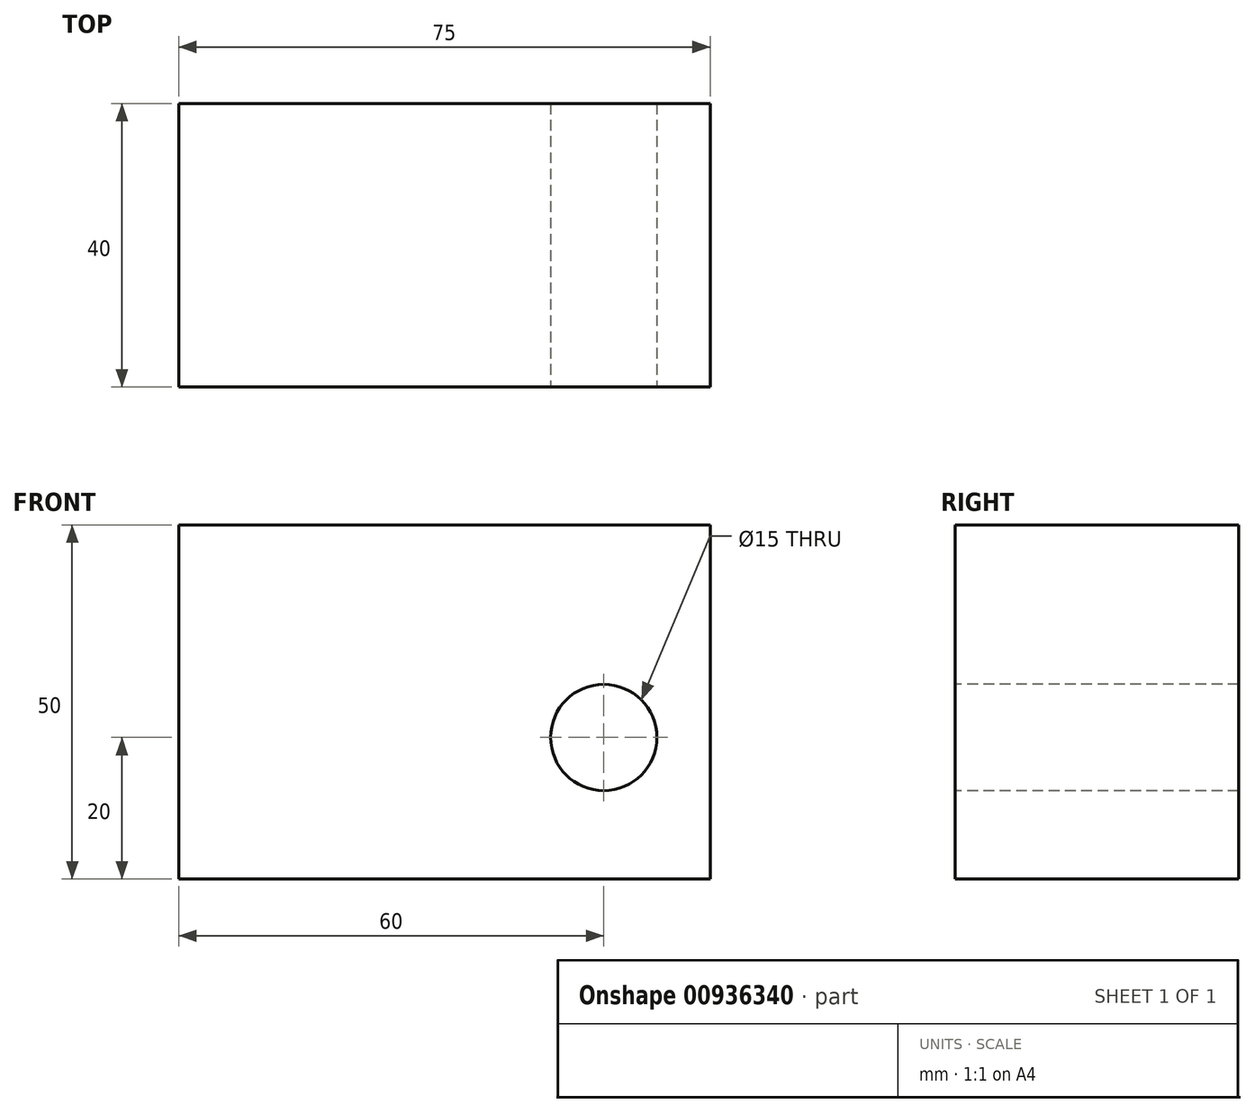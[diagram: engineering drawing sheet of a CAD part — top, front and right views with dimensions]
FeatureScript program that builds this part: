
annotation { "Feature Type Name" : "Feature", "Feature Type Description" : "" }
export const myFeature = defineFeature(function(context is Context, id is Id, definition is map)
    precondition{}
    {
        {
            var Q0;
            Q0=qCreatedBy(makeId("Front.planeOp"),FACE);
            var sketch = newSketch(context, id + "F0", { "sketchPlane" : qUnion([Q0])});
            skLineSegment(sketch, "E0", {"start": v(0, 0) * mm, "end": v(15, 0) * mm});
            skLineSegment(sketch, "E1", {"start": v(15, 0) * mm, "end": v(15, -20) * mm});
            skLineSegment(sketch, "E2", {"start": v(15, -20) * mm, "end": v(0, -20) * mm});
            skLineSegment(sketch, "E3", {"start": v(0, -20) * mm, "end": v(0, 0) * mm});
            skLineSegment(sketch, "E4", {"start": v(0, -20) * mm, "end": v(-60, -20) * mm});
            skLineSegment(sketch, "E5", {"start": v(-60, -20) * mm, "end": v(-60, 30) * mm});
            skLineSegment(sketch, "E6", {"start": v(-60, 30) * mm, "end": v(15, 30) * mm});
            skLineSegment(sketch, "E7", {"start": v(15, 30) * mm, "end": v(15, 0) * mm});
            skSolve(sketch);
        }
        {
            var Q0;
            Q0=makeQuery(id+"F0.imprint","IMPRINT",FACE,{"disambiguationData":[TD([[makeQuery(id+"F0.imprint","IMPRINT",EDGE,{"derivedFrom":sQuery(id+"F0.wireOp",EDGE,"E0")}),1.0]])]});
            var Q1;
            Q1=makeQuery(id+"F0.imprint","IMPRINT",FACE,{"disambiguationData":[TD([[makeQuery(id+"F0.imprint","IMPRINT",EDGE,{"derivedFrom":sQuery(id+"F0.wireOp",EDGE,"E0")}),-1.0]])]});
            extrude(context, id + "F1", {"entities" : qUnion([Q0, Q1]), "depth" : 40 * mm, "offsetDistance" : 25 * mm});
        }
        {
            var Q0;
            Q0=makeQuery(id+"F1.opExtrude","CAP_FACE",FACE,{"disambiguationData":[OSD([sQuery(id+"F0.wireOp",EDGE,"E1"),sQuery(id+"F0.wireOp",EDGE,"E2"),sQuery(id+"F0.wireOp",EDGE,"E4"),sQuery(id+"F0.wireOp",EDGE,"E5"),sQuery(id+"F0.wireOp",EDGE,"E6"),sQuery(id+"F0.wireOp",EDGE,"E7")])],"isStart":false});
            var sketch = newSketch(context, id + "F2", { "sketchPlane" : qUnion([Q0])});
            skCircle(sketch, "E8", {"center": v(0, 0) * mm, "radius": 7.5 * mm});
            skSolve(sketch);
        }
        {
            var Q0;
            Q0 = qSketchRegion(id + "F2", true);
            var Q1;
            Q1=makeQuery(id+"F1.opExtrude","CAP_FACE",FACE,{"disambiguationData":[OSD([sQuery(id+"F0.wireOp",EDGE,"E1"),sQuery(id+"F0.wireOp",EDGE,"E2"),sQuery(id+"F0.wireOp",EDGE,"E4"),sQuery(id+"F0.wireOp",EDGE,"E5"),sQuery(id+"F0.wireOp",EDGE,"E6"),sQuery(id+"F0.wireOp",EDGE,"E7")])],"isStart":true});
            extrude(context, id + "F3", {"entities" : qUnion([Q0]), "operationType" : NewBodyOperationType.REMOVE, "endBound" : BoundingType.UP_TO_SURFACE, "oppositeDirection" : true, "depth" : 40 * mm, "endBoundEntityFace" : qUnion([Q1]), "offsetDistance" : 25 * mm});
        }
    });
